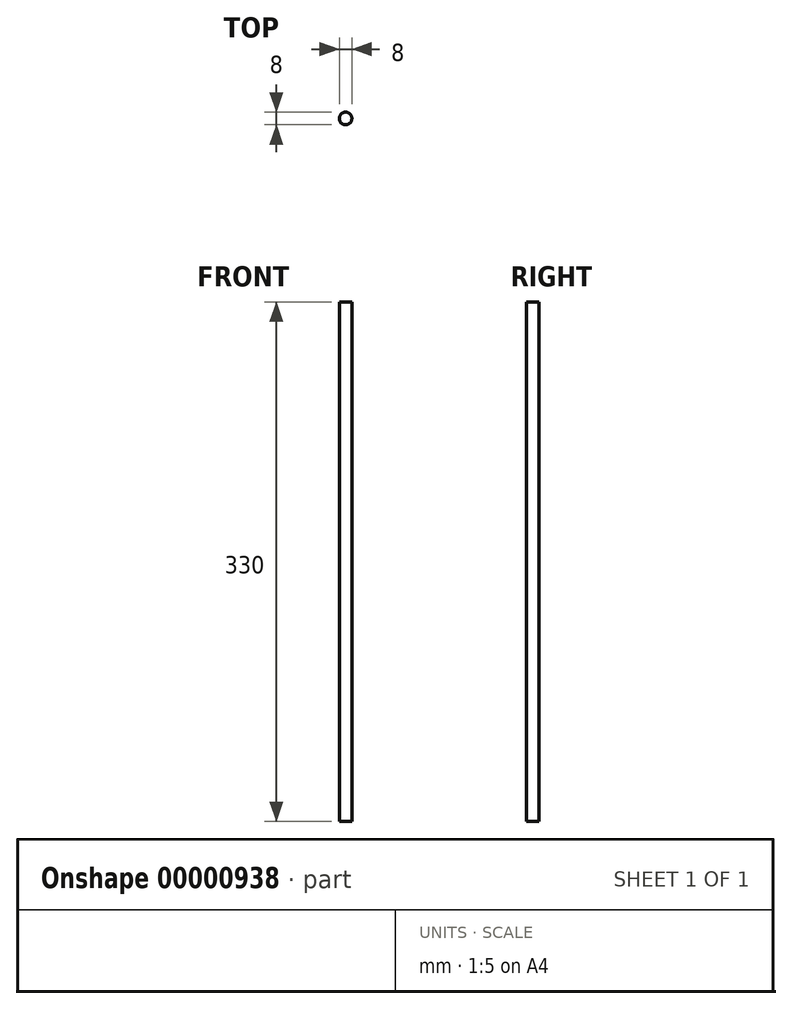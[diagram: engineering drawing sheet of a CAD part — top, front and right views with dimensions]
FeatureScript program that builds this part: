
annotation { "Feature Type Name" : "Feature", "Feature Type Description" : "" }
export const myFeature = defineFeature(function(context is Context, id is Id, definition is map)
    precondition{}
    {
        {
            var Q0;
            Q0=qCreatedBy(makeId("Top.planeOp"),FACE);
            var sketch = newSketch(context, id + "F0", { "sketchPlane" : qUnion([Q0])});
            skCircle(sketch, "E0", {"center": v(0, 0) * mm, "radius": 4 * mm});
            skSolve(sketch);
        }
        {
            var Q0;
            Q0=makeQuery(id+"F0.imprint","IMPRINT",FACE,{"disambiguationData":[TD([[makeQuery(id+"F0.imprint","IMPRINT",EDGE,{"derivedFrom":sQuery(id+"F0.wireOp",EDGE,"E0")}),1.0]])]});
            extrude(context, id + "F1", {"entities" : qUnion([Q0]), "depth" : 330 * mm});
        }
    });
